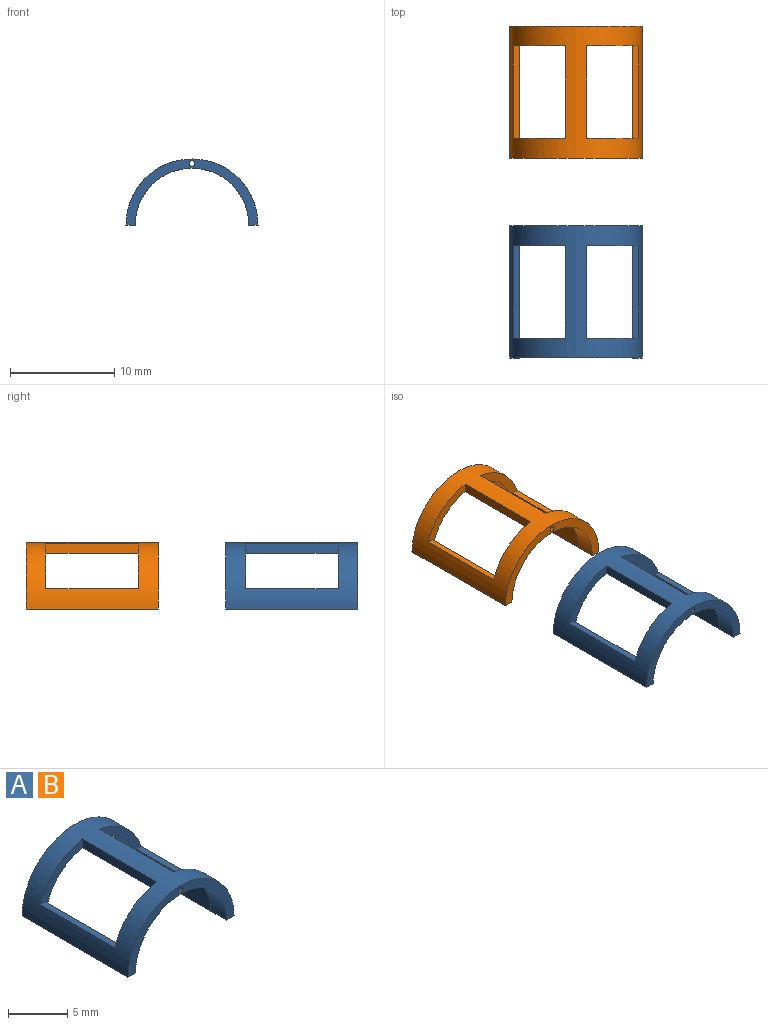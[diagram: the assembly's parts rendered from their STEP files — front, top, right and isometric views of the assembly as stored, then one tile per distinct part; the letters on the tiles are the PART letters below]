
ASSEMBLY  parts=2 mates=1
PART A: 17 faces, bbox 12.7x12.7x6.4 mm
  f0: cylinder r=6.35mm len=12.7mm, axis (0,1,0), area 129.8mm2, adj f2,f3,f4,f5,f6,f8,f9,f10
  f1: cylinder r=5.46mm len=12.7mm, axis (0,1,0), area 83.5mm2, adj f2,f3,f4,f5,f6,f8,f9,f10
  f2: plane 12.7x0.89mm, normal (0,0,-1), area 11.3mm2, adj f0,f1,f4,f5,f7
  f3: plane 12.7x0.89mm, normal (0,0,-1), area 11.3mm2, adj f0,f1,f4,f5,f11
  f4: plane 12.7x6.35mm, normal (0,-1,0), area 16.2mm2, adj f0,f1,f2,f3,f16
  f5: plane 12.7x6.35mm, normal (0,1,0), area 16.2mm2, adj f0,f1,f2,f3,f16
  f6: plane 6.27x5.02mm, normal (0,-1,0), area 5.8mm2, adj f0,f1,f7,f9,f15
  f7: plane 8.89x1.97mm, normal (-1,0,0), area 17.5mm2, adj f2,f6,f8,f15
  f8: plane 6.27x5.02mm, normal (0,1,0), area 5.8mm2, adj f0,f1,f7,f9,f15
  f9: plane 8.89x0.9mm, normal (1,0,0), area 8mm2, adj f0,f1,f6,f8
  f10: plane 6.27x5.02mm, normal (0,1,0), area 5.8mm2, adj f0,f1,f11,f13,f14
  f11: plane 8.89x1.97mm, normal (1,0,0), area 17.5mm2, adj f3,f10,f12,f14
  f12: plane 6.27x5.02mm, normal (0,-1,0), area 5.8mm2, adj f0,f1,f11,f13,f14
  f13: plane 8.89x0.9mm, normal (-1,0,0), area 8mm2, adj f0,f1,f10,f12
  f14: plane 8.89x0.58mm, normal (0,0,1), area 5.1mm2, adj f0,f10,f11,f12
  f15: plane 8.89x0.58mm, normal (0,0,1), area 5.1mm2, adj f0,f6,f7,f8
  f16: cylinder r=0.28mm len=12.7mm, axis (0,-1,0), area 22.4mm2, adj f4,f5
PART B: same geometry as A
PLACE A t=(-1.19,-2.82,16.95)mm
PLACE B t=(-1.19,16.37,16.95)mm
MATE cylindrical B.f16 <-> A.f16  axis (0,-1,0) through (-1.19,3.67,22.85)mm
